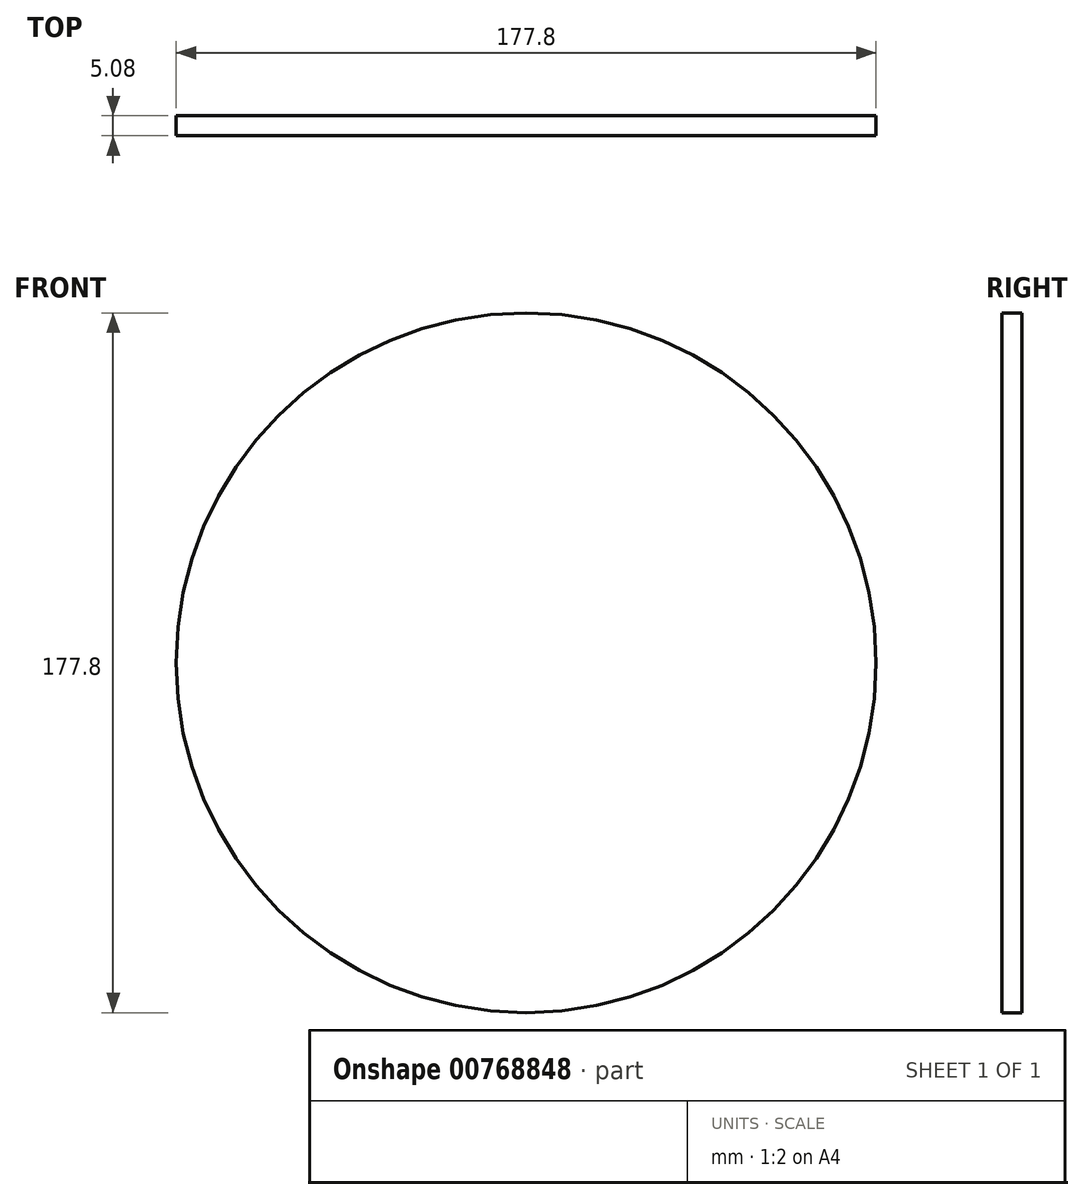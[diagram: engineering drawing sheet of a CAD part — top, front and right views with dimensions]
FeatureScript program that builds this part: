
annotation { "Feature Type Name" : "Feature", "Feature Type Description" : "" }
export const myFeature = defineFeature(function(context is Context, id is Id, definition is map)
    precondition{}
    {
        {
            var Q0;
            Q0=qCreatedBy(makeId("Front.planeOp"),FACE);
            var sketch = newSketch(context, id + "F0", { "sketchPlane" : qUnion([Q0])});
            skCircle(sketch, "E0", {"center": v(0, 0) * mm, "radius": 88.9 * mm});
            skSolve(sketch);
        }
        {
            var Q0;
            Q0 = qSketchRegion(id + "F0", true);
            extrude(context, id + "F1", {"entities" : qUnion([Q0]), "depth" : 5.08 * mm, "offsetDistance" : 25.4 * mm});
        }
    });
